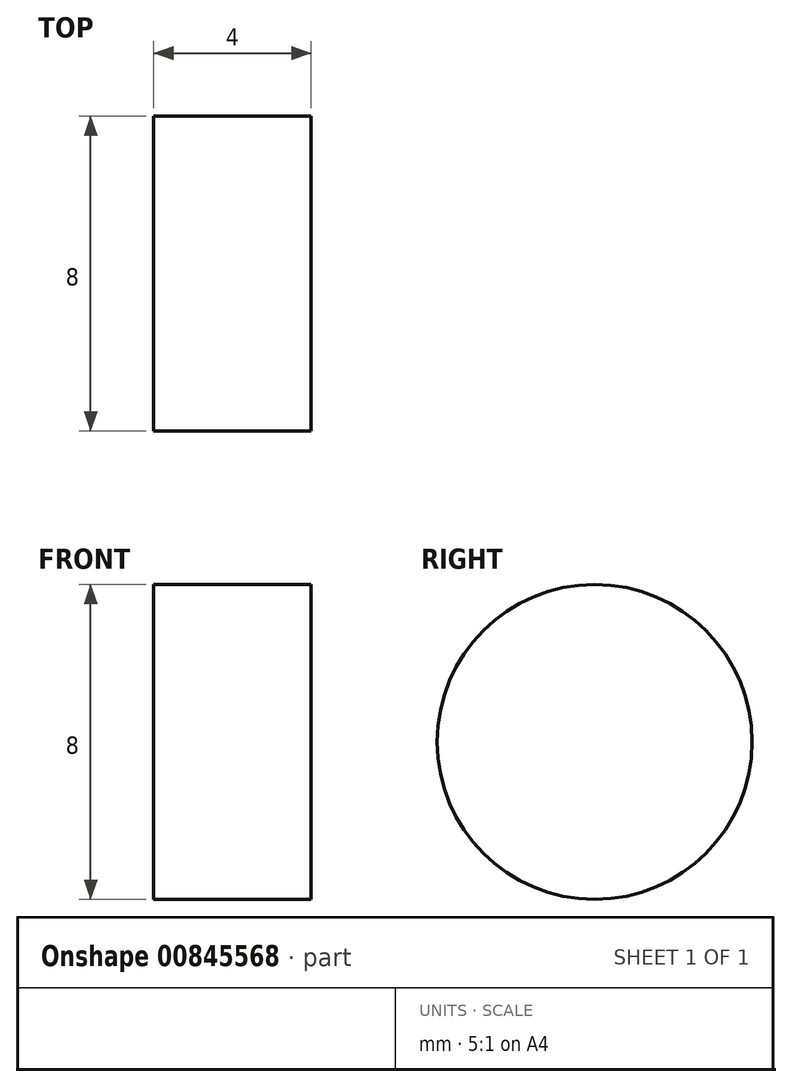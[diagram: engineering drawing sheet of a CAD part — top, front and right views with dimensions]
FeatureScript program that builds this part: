
annotation { "Feature Type Name" : "Feature", "Feature Type Description" : "" }
export const myFeature = defineFeature(function(context is Context, id is Id, definition is map)
    precondition{}
    {
        {
            var Q0;
            Q0=qCreatedBy(makeId("Front.planeOp"),FACE);
            var sketch = newSketch(context, id + "F0", { "sketchPlane" : qUnion([Q0])});
            skLineSegment(sketch, "E0.bottom", {"start": v(2, -2) * mm, "end": v(-2, -2) * mm});
            skLineSegment(sketch, "E0.top", {"start": v(2, 2) * mm, "end": v(-2, 2) * mm});
            skLineSegment(sketch, "E0.left", {"start": v(2, -2) * mm, "end": v(2, 2) * mm});
            skLineSegment(sketch, "E0.right", {"start": v(-2, -2) * mm, "end": v(-2, 2) * mm});
            skPoint(sketch, "E0.middle", {"position": v(0, 0) * mm});
            skSolve(sketch);
        }
        {
            var Q0;
            Q0=makeQuery(id+"F0.imprint","IMPRINT",FACE,{"disambiguationData":[TD([[makeQuery(id+"F0.imprint","IMPRINT",EDGE,{"derivedFrom":sQuery(id+"F0.wireOp",EDGE,"E0.bottom")}),-1.0]])]});
            var Q1;
            Q1=sQuery(id+"F0.wireOp",EDGE,"E0.bottom");
            revolve(context, id + "F1", {"surfaceOperationType" : NewSurfaceOperationType.NEW, "entities" : qUnion([Q0]), "axis" : qUnion([Q1]), "revolveType" : RevolveType.FULL});
        }
    });
